# Revit family: DFM Doors - one leaf door EI 120
name_source: partatom
category: Doors
revit_build: Autodesk Revit 2017 (Build: 20190507_1515(x64)
units: mm (PartAtom-declared; Revit-internal decimal feet)

## family parameters
Always vertical = Yes
Cut with Voids When Loaded = No
Host = Wall
OmniClass Number = 23.30.10.00
OmniClass Title = Doors
Room Calculation Point = Yes
Shared = No

## types (1)
- 2018x916 internal frame
    Clear opening height = 2018 mm  [stored 6.62073 ft]
    Clear opening height. Limiting dimensions = ok
    Clear opening width = 916 mm  [stored 3.00525 ft]
    Clear opening width. Limiting dimensions = ok
    Clear opening width. Remarks regarding escape route = ok
    Corner frame = No
    Embracing frame = No
    Escape doors = No
    Fire Rating = EI 120
    Frame to frame width = 922 mm  [stored 3.02493 ft]
    Function = Interior
    Glazing thickness = 62 mm  [stored 0.203412 ft]
    Height = 2101 mm  [stored 6.89304 ft]
    Height of the door leaf = 2050 mm  [stored 6.72572 ft]
    Internal frame = Yes
    Manufacturer = DFM Doors sp. z o. o.
    Material of door closer = DFM Doors - aluminium
    Material of door frame = DFM Doors - zinc coated steel
    Material of door leaf = DFM Doors - zinc coated steel
    Material of drip cap = DFM Doors - zinc coated steel
    Material of glass = DFM Doors - glazing
    Material of glass framing = DFM Doors - zinc coated steel
    Material of hinges = DFM Doors - stainless steel
    Material of ironmongery = DFM Doors - aluminium
    Model = DFM DS 120 - 1
    Offset of drip cap = 0 mm  [stored 0 ft]
    Offset of the door leaf = 58 mm  [stored 0.190289 ft]
    Offset of the fitting = 419.5 mm
    Rough Height = 2101 mm  [stored 6.89304 ft]
    Rough Width = 1088 mm  [stored 3.56955 ft]
    Thickness = 65 mm  [stored 0.213255 ft]
    Type of frame = 2
    URL = https://www.dfm-europe.eu
    Wall Closure = By host
    Width = 1088 mm  [stored 3.56955 ft]
    Width of door leaf = 1003 mm  [stored 3.29068 ft]
    Width of door leaf. Remark regarding escape route = ok

note: [stored X ft] marks values corroborated as IEEE doubles in the binary element streams (Revit-internal decimal feet)
